# Revit family: Hydraulic Buffer
name_source: partatom
category: Mechanical Equipment
units: mm (PartAtom-declared; Revit-internal decimal feet)

## family parameters
Always vertical = Yes
Cut with Voids When Loaded = No
Maintain Annotation Orientation = No
OmniClass Number = 23.75.00.00
OmniClass Title = Climate Control (HVAC)
Part Type = Normal
Room Calculation Point = No
Round Connector Dimension = Use Diameter
Shared = No
Work Plane-Based = No

## types (1)
- Hydraulic Buffer
    Cylinder Diameter = 108 mm  [stored 0.354331 ft]
    Cylinder Height = 290 mm  [stored 0.951444 ft]
    Default Elevation = 0 mm  [stored 0 ft]
    LiftBuffer_FixedToCar = Yes
    LiftBuffer_ImpactMassRange = 3000
    LiftBuffer_RatedSpeed = 2.0 m/s
    LiftBuffer_Stroke = 100
    Mounting plate Length = 200 mm  [stored 0.656168 ft]
    Mounting plate thickness = 20 mm  [stored 0.0656168 ft]
    Mounting plate width = 150 mm
    Stroke Diameter = 75 mm
    buffer Height = 580 mm  [stored 1.90289 ft]

note: [stored X ft] marks values corroborated as IEEE doubles in the binary element streams (Revit-internal decimal feet)

## geometry (parser evidence)
native form markers: Sweep x3
no freeform markers — native parametric forms only
